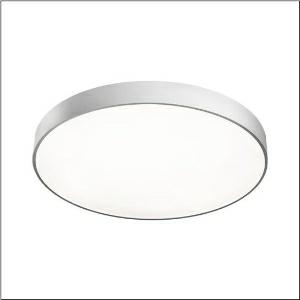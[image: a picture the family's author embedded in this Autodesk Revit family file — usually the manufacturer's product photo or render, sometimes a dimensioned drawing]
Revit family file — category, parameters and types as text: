
# Revit family: round_21_l_51mr38fd0321s
name_source: partatom
category: Lighting Fixtures
units: mm (PartAtom-declared; Revit-internal decimal feet)

## family parameters
Cut with Voids When Loaded = No
Host = Face
Light Source = No
Part Type = Normal
Room Calculation Point = No
Round Connector Dimension = Use Diameter
Shared = No

## types (1)
- Round 21 L (1 x LED, 13590 lm, 97 W, 3000K)
    Apparent Load = 97 VA
    CIE Flux Codes = 49 80 96 100 100
    Color Rendering = 80
    Color Temperature = 3000K
    Default Elevation = 1800 mm
    Description = Round 21 L, wall and ceiling luminaire, primary optical cover: cover, of PMMA, opal, light emission: direct distribution, primary light characteristic: symmetric, installation type: suspended mounting, surface-mounted, LED, rated luminous flux: 13.590lm, luminous efficacy: 140lm/W, light colour: 830, colour temperature: 3000K, control gear: DALI 2, with terminal, 5-pole, mains connection: 230V, AC, 50/60Hz, rated input power: 97W, housing, of aluminium, coated, silver, diameter: 850mm, height: 62mm, protection rating (complete): IP40, insulation class (complete): insulation class I (protective earthing), certification: CE, impact resistance: IK04, permissible operating ambient temperature: -10..+35°C, packaging unit: 1 piece
    Height = 87 mm
    Lamp = 1 x LED
    Lamp Light Flux = 13590 lm
    Lamp Power = 97 W
    Lamp count = 1
    Length = 850 mm
    Luminous efficacy = 140 lm/W
    Manufacturer = Siteco
    ModVariant = No
    Model = 51MR38FD0321S
    Mounting Place = Ceiling
    Mounting Type = Surface mounted
    Number of Poles = 1
    OnlyDefault = Yes
    Power Factor = 1
    Product Name = Round 21 L
    Product group = wall and ceiling luminaire | ceiling mounted
    ProductGroupID = 305
    Protection Class = Protection class I
    Protection Degree = IP 40
    RLX_Detail_Level = 1
    RLX_Emergency_Light_Flux = 0 lm
    RLX_Emergency_Type = 0
    RLX_Emergency_Type_DB = No
    RlxData = <blob elided: 20249 chars, md5=c270ed35>
    Socket = socket
    Standby Power = 0 W
    System Light Flux = 13590 lm
    System Power = 97 W
    Type Comments = Product without accessories
    Type Image = l_1258324.jpg
    URL = http://relux.com
    VarID = ---
    Voltage = 0 V
    Weight = 0.00 kg
    Width = 0 mm  [stored 0 ft]

note: [stored X ft] marks values corroborated as IEEE doubles in the binary element streams (Revit-internal decimal feet)

## geometry (parser evidence)
native form markers: Blend x4, Sweep x12
no freeform markers — native parametric forms only
